# Revit family: Bernhardt_Design-Tables-Freestanding-Frame-Block_36h-Blueprint
name_source: partatom
category: Furniture
revit_build: Autodesk Revit 2016 (Build: 20150714_1515(x64)
units: mm (PartAtom-declared; Revit-internal decimal feet)

## family parameters
Always vertical = Yes
Cut with Voids When Loaded = No
OmniClass Number = 23.40.20.00
OmniClass Title = General Furniture and Specialties
Room Calculation Point = No
Shared = No
Work Plane-Based = No

## types (9) — shared parameters
BlackPaint = Black Paint
Blueprint Gray = Blueprint Gray
LegDistance = 20"
LegHeight = 35"
Manufacturer = Bernhardt Design
Model = Blueprint
RailCap = 0"
RailCapFront = 2"
TableTop = <By Category>
TableTopHeight = 35"
TotalHeight = 36"
URL = http://www.bernhardtdesign.com
Wood = <By Category>

## per-type parameters (varying)
| type | CapDistance_left | CapDistance_right | Railing_bottom | Railing_top | TableDepth | TableWidth_left | TableWidth_right | TotalDepth | TotalWidth |
| BPS-BGC-AC | 33 1/2" | 23 1/2" | -31 1/2" | 31 1/2" | 24" | 45" | 27 1/2" | 48" | 72" |
| BPS-BGA-AC | 33 1/2" | 23 1/2" | -31 1/2" | 31 1/2" | 18" | 45" | 27 1/2" | 36" | 72" |
| BPS-BKC-AC | 35 1/2" | 35 1/2" | -33 1/2" | 33 1/2" | 24" | 57" | 39 1/2" | 48" | 96" |
| BPS-BOC-AC | 47 1/2" | 47 1/2" | -45 1/2" | 45 1/2" | 24" | 69" | 51 1/2" | 48" | 120" |
| BPS-BKA-AC | 35 1/2" | 35 1/2" | -33 1/2" | 33 1/2" | 18" | 57" | 39 1/2" | 36" | 96" |
| BPS-BGB-AC | 33 1/2" | 23 1/2" | -31 1/2" | 31 1/2" | 21" | 45" | 27 1/2" | 42" | 72" |
| BPS-BKB-AC | 35 1/2" | 35 1/2" | -33 1/2" | 33 1/2" | 21" | 57" | 39 1/2" | 42" | 96" |
| BPS-BOA-AC | 47 1/2" | 47 1/2" | -45 1/2" | 45 1/2" | 18" | 69" | 51 1/2" | 36" | 120" |
| BPS-BOB-AC | 47 1/2" | 47 1/2" | -45 1/2" | 45 1/2" | 21" | 69" | 51 1/2" | 42" | 120" |

note: column(s) folded — value = type name in every type: Catalog, SKU

## geometry (parser evidence)
native form markers: Blend x4, Sweep x1
no freeform markers — native parametric forms only
